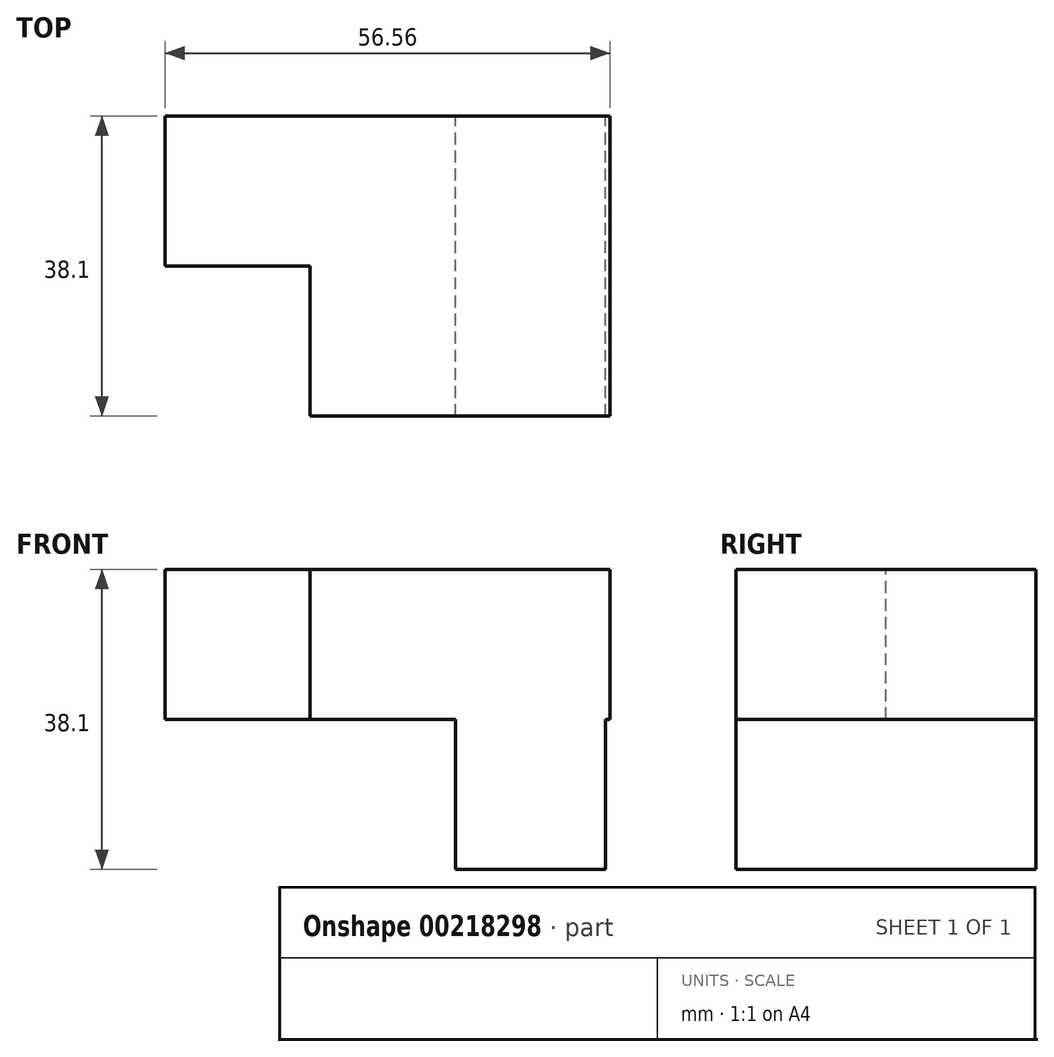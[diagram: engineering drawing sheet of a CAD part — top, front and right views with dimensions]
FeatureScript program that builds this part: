
annotation { "Feature Type Name" : "Feature", "Feature Type Description" : "" }
export const myFeature = defineFeature(function(context is Context, id is Id, definition is map)
    precondition{}
    {
        {
            var Q0;
            Q0=qCreatedBy(makeId("Front.planeOp"),FACE);
            var sketch = newSketch(context, id + "F0", { "sketchPlane" : qUnion([Q0])});
            skLineSegment(sketch, "E0", {"start": v(-70.39, 0) * mm, "end": v(-70.39, 19.05) * mm});
            skLineSegment(sketch, "E1", {"start": v(-70.39, 19.05) * mm, "end": v(-51.34, 19.05) * mm});
            skLineSegment(sketch, "E2", {"start": v(-51.34, 19.05) * mm, "end": v(-51.34, 0) * mm});
            skLineSegment(sketch, "E3", {"start": v(-51.34, 0) * mm, "end": v(-70.39, 0) * mm});
            skSolve(sketch);
        }
        {
            var Q0;
            Q0=makeQuery(id+"F0.imprint","IMPRINT",FACE,{"disambiguationData":[TD([[makeQuery(id+"F0.imprint","IMPRINT",EDGE,{"derivedFrom":sQuery(id+"F0.wireOp",EDGE,"E0")}),-1.0]])]});
            extrude(context, id + "F1", {"entities" : qUnion([Q0]), "depth" : 19.05 * mm});
        }
        {
            var Q0;
            Q0=qCreatedBy(makeId("Front.planeOp"),FACE);
            var sketch = newSketch(context, id + "F2", { "sketchPlane" : qUnion([Q0])});
            skLineSegment(sketch, "E4", {"start": v(-51.93, 19.05) * mm, "end": v(-13.83, 19.05) * mm});
            skLineSegment(sketch, "E5", {"start": v(-13.83, 19.05) * mm, "end": v(-13.83, 0) * mm});
            skLineSegment(sketch, "E6", {"start": v(-13.83, 0) * mm, "end": v(-51.93, 0) * mm});
            skLineSegment(sketch, "E7", {"start": v(-51.93, 0) * mm, "end": v(-51.93, 19.05) * mm});
            skSolve(sketch);
        }
        {
            var Q0;
            Q0=makeQuery(id+"F2.imprint","IMPRINT",FACE,{"disambiguationData":[TD([[makeQuery(id+"F2.imprint","IMPRINT",EDGE,{"derivedFrom":sQuery(id+"F2.wireOp",EDGE,"E4")}),-1.0]])]});
            extrude(context, id + "F3", {"entities" : qUnion([Q0]), "operationType" : NewBodyOperationType.ADD, "depth" : 38.1 * mm});
        }
        {
            var Q0;
            Q0=qCreatedBy(makeId("Front.planeOp"),FACE);
            var sketch = newSketch(context, id + "F4", { "sketchPlane" : qUnion([Q0])});
            skLineSegment(sketch, "E8", {"start": v(-14.44, 0) * mm, "end": v(-14.44, -19.05) * mm});
            skLineSegment(sketch, "E9", {"start": v(-14.44, -19.05) * mm, "end": v(-33.5, -19.05) * mm});
            skLineSegment(sketch, "E10", {"start": v(-33.5, -19.05) * mm, "end": v(-33.5, 0) * mm});
            skLineSegment(sketch, "E11", {"start": v(-33.5, 0) * mm, "end": v(-14.44, 0) * mm});
            skSolve(sketch);
        }
        {
            var Q0;
            Q0=makeQuery(id+"F4.imprint","IMPRINT",FACE,{"disambiguationData":[TD([[makeQuery(id+"F4.imprint","IMPRINT",EDGE,{"derivedFrom":sQuery(id+"F4.wireOp",EDGE,"E8")}),-1.0]])]});
            extrude(context, id + "F5", {"entities" : qUnion([Q0]), "operationType" : NewBodyOperationType.ADD, "depth" : 38.1 * mm});
        }
    });
